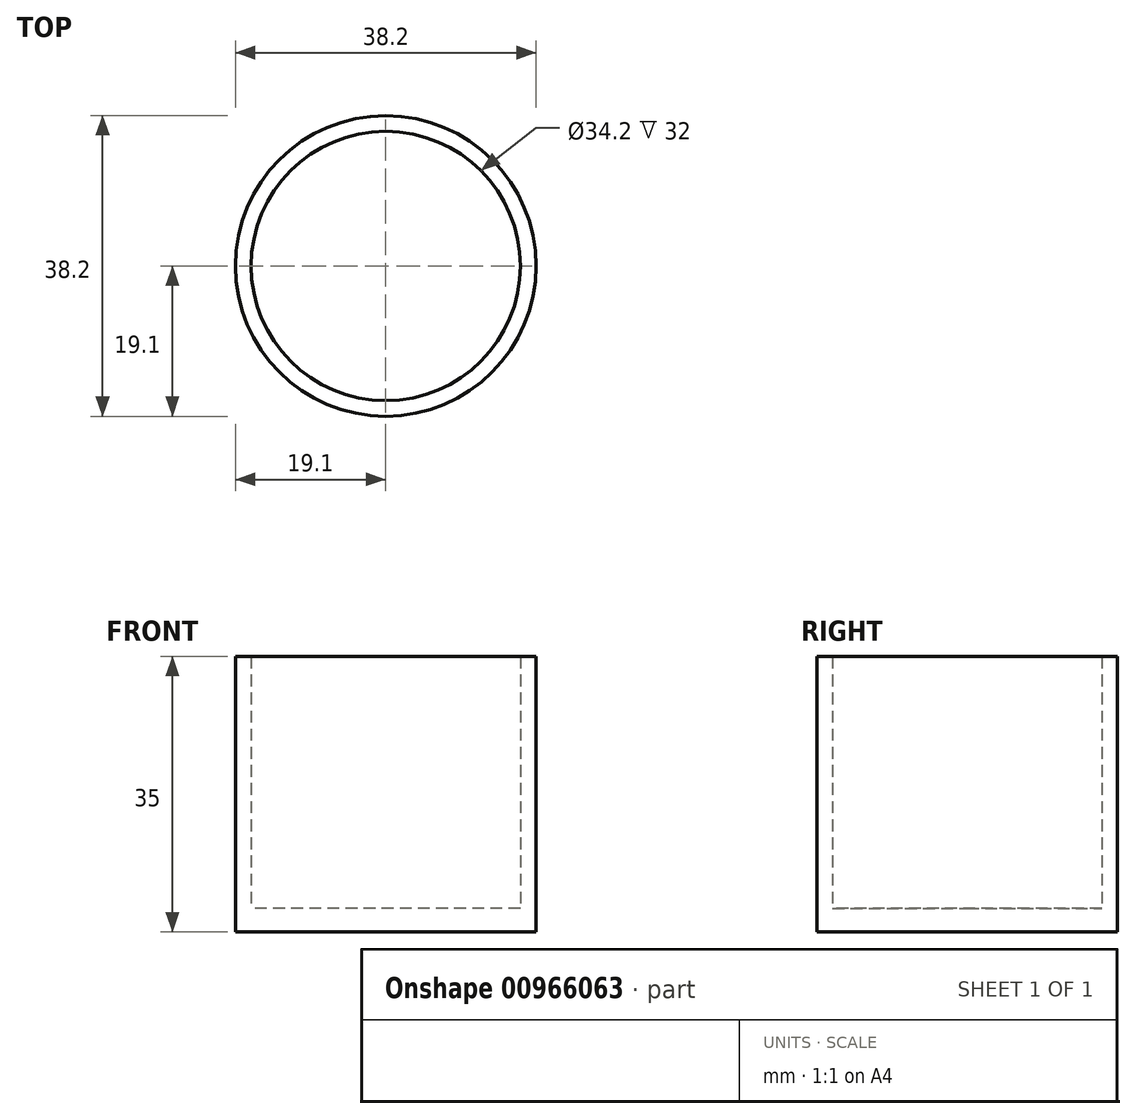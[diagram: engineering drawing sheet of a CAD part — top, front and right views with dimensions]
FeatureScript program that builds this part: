
annotation { "Feature Type Name" : "Feature", "Feature Type Description" : "" }
export const myFeature = defineFeature(function(context is Context, id is Id, definition is map)
    precondition{}
    {
        {
            var Q0;
            Q0=qCreatedBy(makeId("Top.planeOp"),FACE);
            var sketch = newSketch(context, id + "F0", { "sketchPlane" : qUnion([Q0])});
            skCircle(sketch, "E0", {"center": v(0, 0) * mm, "radius": 17.1 * mm});
            skCircle(sketch, "E1", {"center": v(0, 0) * mm, "radius": 19.1 * mm});
            skSolve(sketch);
        }
        {
            var Q0;
            Q0=makeQuery(id+"F0.imprint","IMPRINT",FACE,{"disambiguationData":[TD([[makeQuery(id+"F0.imprint","IMPRINT",EDGE,{"derivedFrom":sQuery(id+"F0.wireOp",EDGE,"E0")}),1.0]])]});
            var Q1;
            Q1=makeQuery(id+"F0.imprint","IMPRINT",FACE,{"disambiguationData":[TD([[makeQuery(id+"F0.imprint","IMPRINT",EDGE,{"derivedFrom":sQuery(id+"F0.wireOp",EDGE,"E0")}),-1.0]])]});
            extrude(context, id + "F1", {"entities" : qUnion([Q0, Q1]), "depth" : 3 * mm, "offsetDistance" : 25 * mm});
        }
        {
            var Q0;
            Q0=makeQuery(id+"F0.imprint","IMPRINT",FACE,{"disambiguationData":[TD([[makeQuery(id+"F0.imprint","IMPRINT",EDGE,{"derivedFrom":sQuery(id+"F0.wireOp",EDGE,"E0")}),-1.0]])]});
            extrude(context, id + "F2", {"entities" : qUnion([Q0]), "operationType" : NewBodyOperationType.ADD, "depth" : (32 + 3) * mm, "offsetDistance" : 25 * mm});
        }
    });
